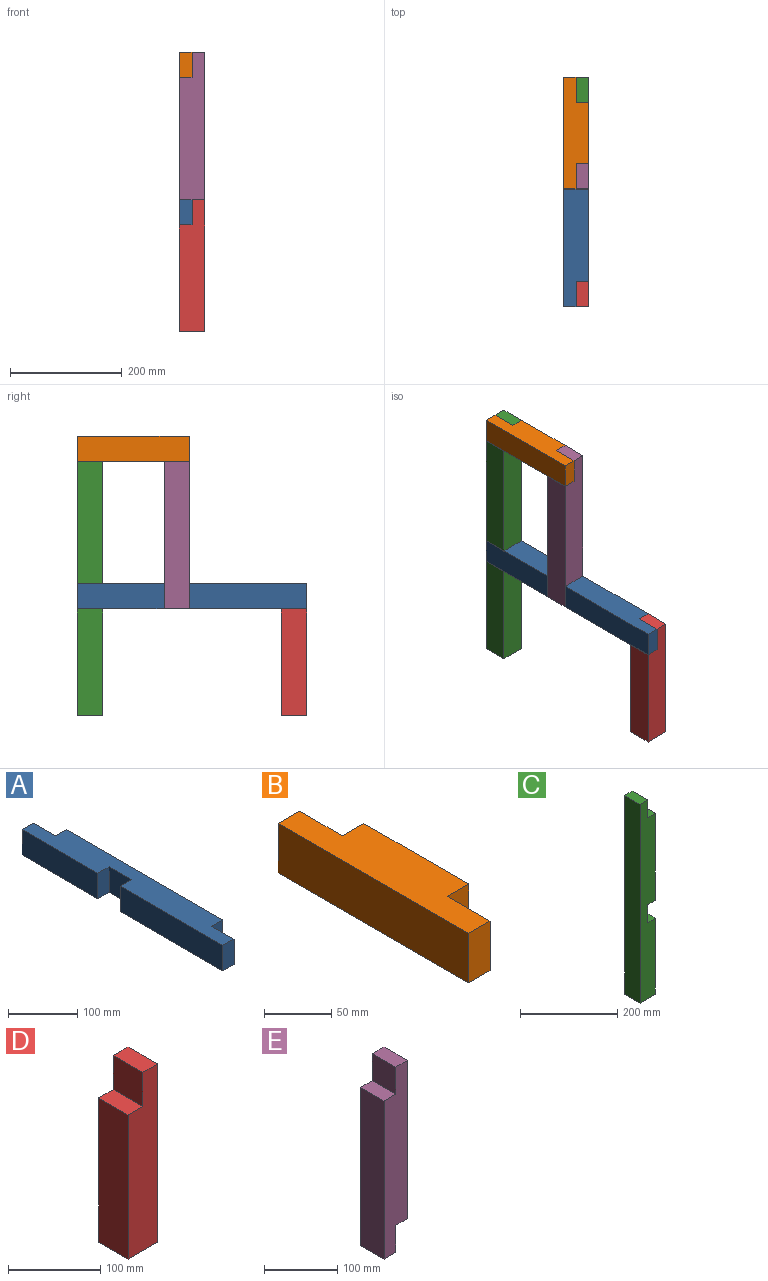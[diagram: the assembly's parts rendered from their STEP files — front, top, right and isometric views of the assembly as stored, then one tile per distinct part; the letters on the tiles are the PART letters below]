
ASSEMBLY  parts=5 mates=4
PART A: 14 faces, bbox 45x410x45 mm
  f0: plane 155x45mm, normal (-1,0,0), area 6975mm2, adj f1,f3,f4,f12
  f1: plane 410x45mm, normal (0,0,1), area 15412.5mm2, adj f0,f2,f4,f5,f6,f7,f8,f9
  f2: plane 45x22.5mm, normal (0,-1,0), area 1012.5mm2, adj f1,f3,f6,f8
  f3: plane 410x45mm, normal (0,0,-1), area 15412.5mm2, adj f0,f2,f4,f5,f6,f7,f8,f9
  f4: plane 45x22.5mm, normal (0,1,0), area 1012.5mm2, adj f0,f1,f3,f10
  f5: plane 320x45mm, normal (1,0,0), area 14400mm2, adj f1,f3,f7,f9
  f6: plane 210x45mm, normal (-1,0,0), area 9450mm2, adj f1,f2,f3,f11
  f7: plane 45x22.5mm, normal (0,-1,0), area 1012.5mm2, adj f1,f3,f5,f8
  f8: plane 45x45mm, normal (1,0,0), area 2025mm2, adj f1,f2,f3,f7
  f9: plane 45x22.5mm, normal (0,1,0), area 1012.5mm2, adj f1,f3,f5,f10
  f10: plane 45x45mm, normal (1,0,0), area 2025mm2, adj f1,f3,f4,f9
  f11: plane 45x22.5mm, normal (0,1,0), area 1012.5mm2, adj f1,f3,f6,f13
  f12: plane 45x22.5mm, normal (0,-1,0), area 1012.5mm2, adj f0,f1,f3,f13
  f13: plane 45x45mm, normal (-1,0,0), area 2025mm2, adj f1,f3,f11,f12
PART B: 10 faces, bbox 45x200x45 mm
  f0: plane 45x22.5mm, normal (0,-1,0), area 1012.5mm2, adj f1,f3,f5,f7
  f1: plane 200x45mm, normal (0,0,-1), area 6975mm2, adj f0,f2,f4,f5,f6,f7,f8,f9
  f2: plane 45x22.5mm, normal (0,1,0), area 1012.5mm2, adj f1,f3,f5,f9
  f3: plane 200x45mm, normal (0,0,1), area 6975mm2, adj f0,f2,f4,f5,f6,f7,f8,f9
  f4: plane 110x45mm, normal (1,0,0), area 4950mm2, adj f1,f3,f6,f8
  f5: plane 200x45mm, normal (-1,0,0), area 9000mm2, adj f0,f1,f2,f3
  f6: plane 45x22.5mm, normal (0,-1,0), area 1012.5mm2, adj f1,f3,f4,f7
  f7: plane 45x45mm, normal (1,0,0), area 2025mm2, adj f0,f1,f3,f6
  f8: plane 45x22.5mm, normal (0,1,0), area 1012.5mm2, adj f1,f3,f4,f9
  f9: plane 45x45mm, normal (1,0,0), area 2025mm2, adj f1,f2,f3,f8
PART C: 12 faces, bbox 45x45x500 mm
  f0: plane 45x22.5mm, normal (0,0,1), area 1012.5mm2, adj f2,f4,f6,f11
  f1: plane 219x45mm, normal (1,0,0), area 9855mm2, adj f2,f4,f7,f10
  f2: plane 500x45mm, normal (0,-1,0), area 20475mm2, adj f0,f1,f3,f5,f6,f7,f8,f9
  f3: plane 45x45mm, normal (0,0,-1), area 2025mm2, adj f2,f4,f5,f6
  f4: plane 500x45mm, normal (0,1,0), area 20475mm2, adj f0,f1,f3,f5,f6,f7,f8,f9
  f5: plane 191x45mm, normal (1,0,0), area 8595mm2, adj f2,f3,f4,f8
  f6: plane 500x45mm, normal (-1,0,0), area 22500mm2, adj f0,f2,f3,f4
  f7: plane 45x22.5mm, normal (0,0,-1), area 1012.5mm2, adj f1,f2,f4,f9
  f8: plane 45x22.5mm, normal (0,0,1), area 1012.5mm2, adj f2,f4,f5,f9
  f9: plane 45x45mm, normal (1,0,0), area 2025mm2, adj f2,f4,f7,f8
  f10: plane 45x22.5mm, normal (0,0,1), area 1012.5mm2, adj f1,f2,f4,f11
  f11: plane 45x45mm, normal (1,0,0), area 2025mm2, adj f0,f2,f4,f10
PART D: 8 faces, bbox 45x45x236 mm
  f0: plane 191x45mm, normal (-1,0,0), area 8595mm2, adj f1,f3,f5,f6
  f1: plane 236x45mm, normal (0,-1,0), area 9607.5mm2, adj f0,f2,f4,f5,f6,f7
  f2: plane 236x45mm, normal (1,0,0), area 10620mm2, adj f1,f3,f4,f5
  f3: plane 236x45mm, normal (0,1,0), area 9607.5mm2, adj f0,f2,f4,f5,f6,f7
  f4: plane 45x22.5mm, normal (0,0,1), area 1012.5mm2, adj f1,f2,f3,f7
  f5: plane 45x45mm, normal (0,0,-1), area 2025mm2, adj f0,f1,f2,f3
  f6: plane 45x22.5mm, normal (0,0,1), area 1012.5mm2, adj f0,f1,f3,f7
  f7: plane 45x45mm, normal (-1,0,0), area 2025mm2, adj f1,f3,f4,f6
PART E: 10 faces, bbox 45x45x309 mm
  f0: plane 264x45mm, normal (1,0,0), area 11880mm2, adj f1,f4,f5,f8
  f1: plane 309x45mm, normal (0,1,0), area 11880mm2, adj f0,f2,f3,f5,f6,f7,f8,f9
  f2: plane 45x22.5mm, normal (0,0,-1), area 1012.5mm2, adj f1,f3,f4,f9
  f3: plane 264x45mm, normal (-1,0,0), area 11880mm2, adj f1,f2,f4,f6
  f4: plane 309x45mm, normal (0,-1,0), area 11880mm2, adj f0,f2,f3,f5,f6,f7,f8,f9
  f5: plane 45x22.5mm, normal (0,0,1), area 1012.5mm2, adj f0,f1,f4,f7
  f6: plane 45x22.5mm, normal (0,0,1), area 1012.5mm2, adj f1,f3,f4,f7
  f7: plane 45x45mm, normal (-1,0,0), area 2025mm2, adj f1,f4,f5,f6
  f8: plane 45x22.5mm, normal (0,0,-1), area 1012.5mm2, adj f0,f1,f4,f9
  f9: plane 45x45mm, normal (1,0,0), area 2025mm2, adj f1,f2,f4,f8
PLACE A rot(axis=(1,0,0),0deg) t=(0,-240,-264)mm
PLACE B t=(0,-30,0)mm
PLACE C rot(axis=(0,0,1),180deg) t=(45,170,-455)mm
PLACE D rot(axis=(1,0,0),0deg) t=(0,-240,-455)mm
PLACE E rot(axis=(0,0,-1),0deg) t=(0,-30,-264)mm
MATE fastened D.f7 <-> A.f8  axis (-1,0,0) through (22.5,-217.5,-241.5)mm
MATE fastened A.f10 <-> C.f9  axis (1,0,0) through (22.5,147.5,-241.5)mm
MATE fastened C.f11 <-> B.f9  axis (-1,0,0) through (22.5,147.5,22.5)mm
MATE fastened E.f9 <-> A.f13  axis (1,0,0) through (22.5,-7.5,-241.5)mm
